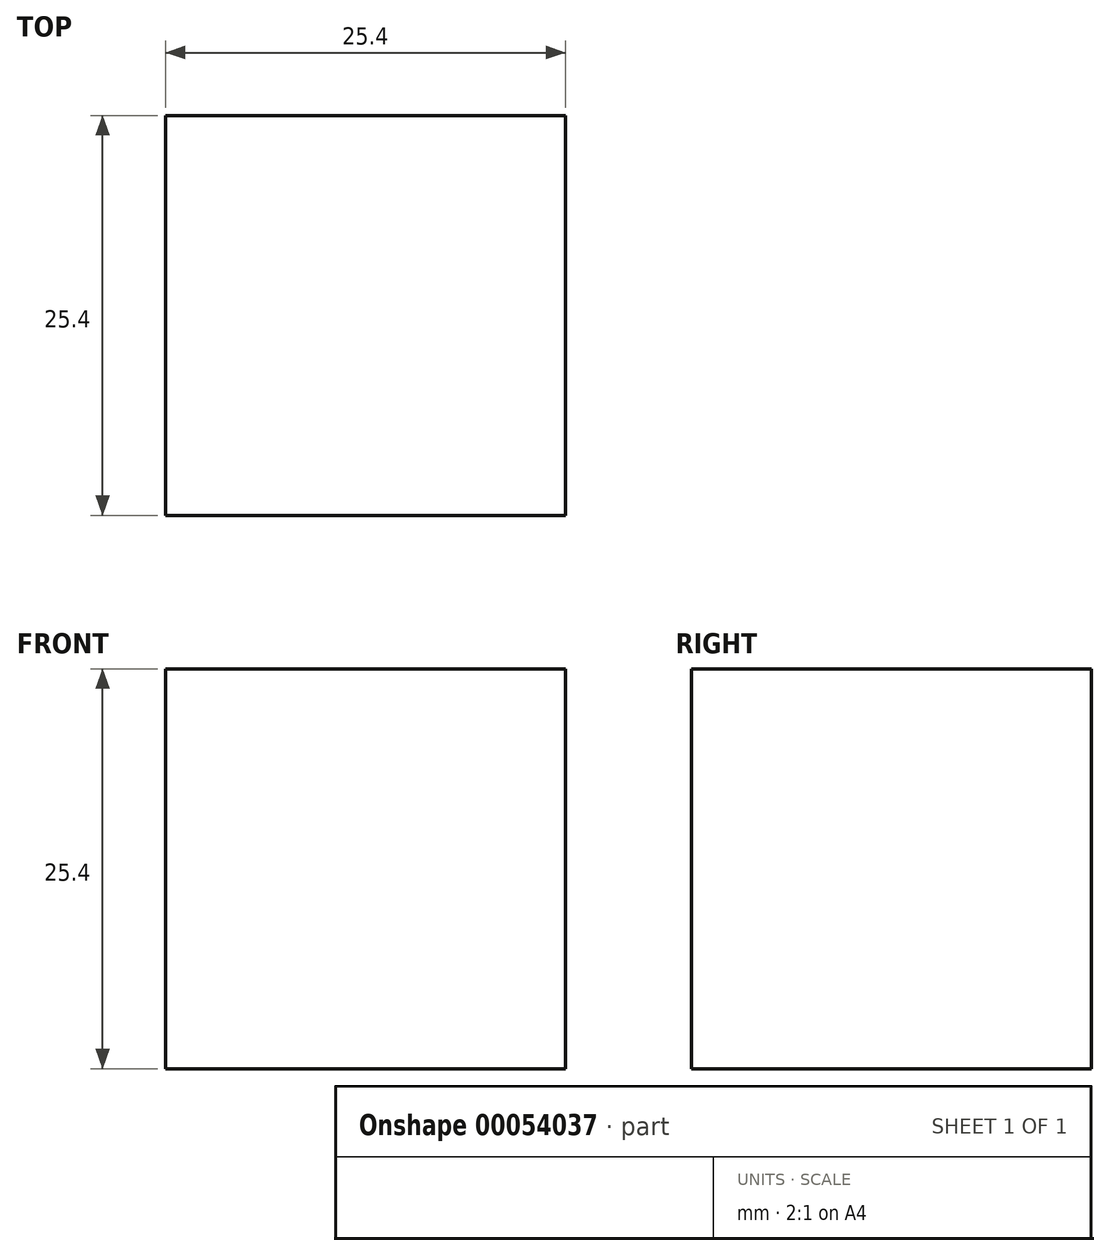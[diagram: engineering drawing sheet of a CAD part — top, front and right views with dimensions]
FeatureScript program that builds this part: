
annotation { "Feature Type Name" : "Feature", "Feature Type Description" : "" }
export const myFeature = defineFeature(function(context is Context, id is Id, definition is map)
    precondition{}
    {
        {
            var Q0;
            Q0=qCreatedBy(makeId("Top.planeOp"),FACE);
            var sketch = newSketch(context, id + "F0", { "sketchPlane" : qUnion([Q0])});
            skLineSegment(sketch, "E0.rect.bottom", {"start": v(12.7, 12.7) * mm, "end": v(-12.7, 12.7) * mm});
            skLineSegment(sketch, "E0.rect.top", {"start": v(12.7, -12.7) * mm, "end": v(-12.7, -12.7) * mm});
            skLineSegment(sketch, "E0.rect.left", {"start": v(12.7, 12.7) * mm, "end": v(12.7, -12.7) * mm});
            skLineSegment(sketch, "E0.rect.right", {"start": v(-12.7, 12.7) * mm, "end": v(-12.7, -12.7) * mm});
            skPoint(sketch, "E0.rect.middle", {"position": v(0, 0) * mm});
            skSolve(sketch);
        }
        {
            var Q0;
            Q0 = qSketchRegion(id + "F0", true);
            extrude(context, id + "F1", {"entities" : qUnion([Q0]), "depth" : 12.7 * mm, "hasSecondDirection" : true, "secondDirectionOppositeDirection" : true, "secondDirectionDepth" : 12.7 * mm});
        }
    });
